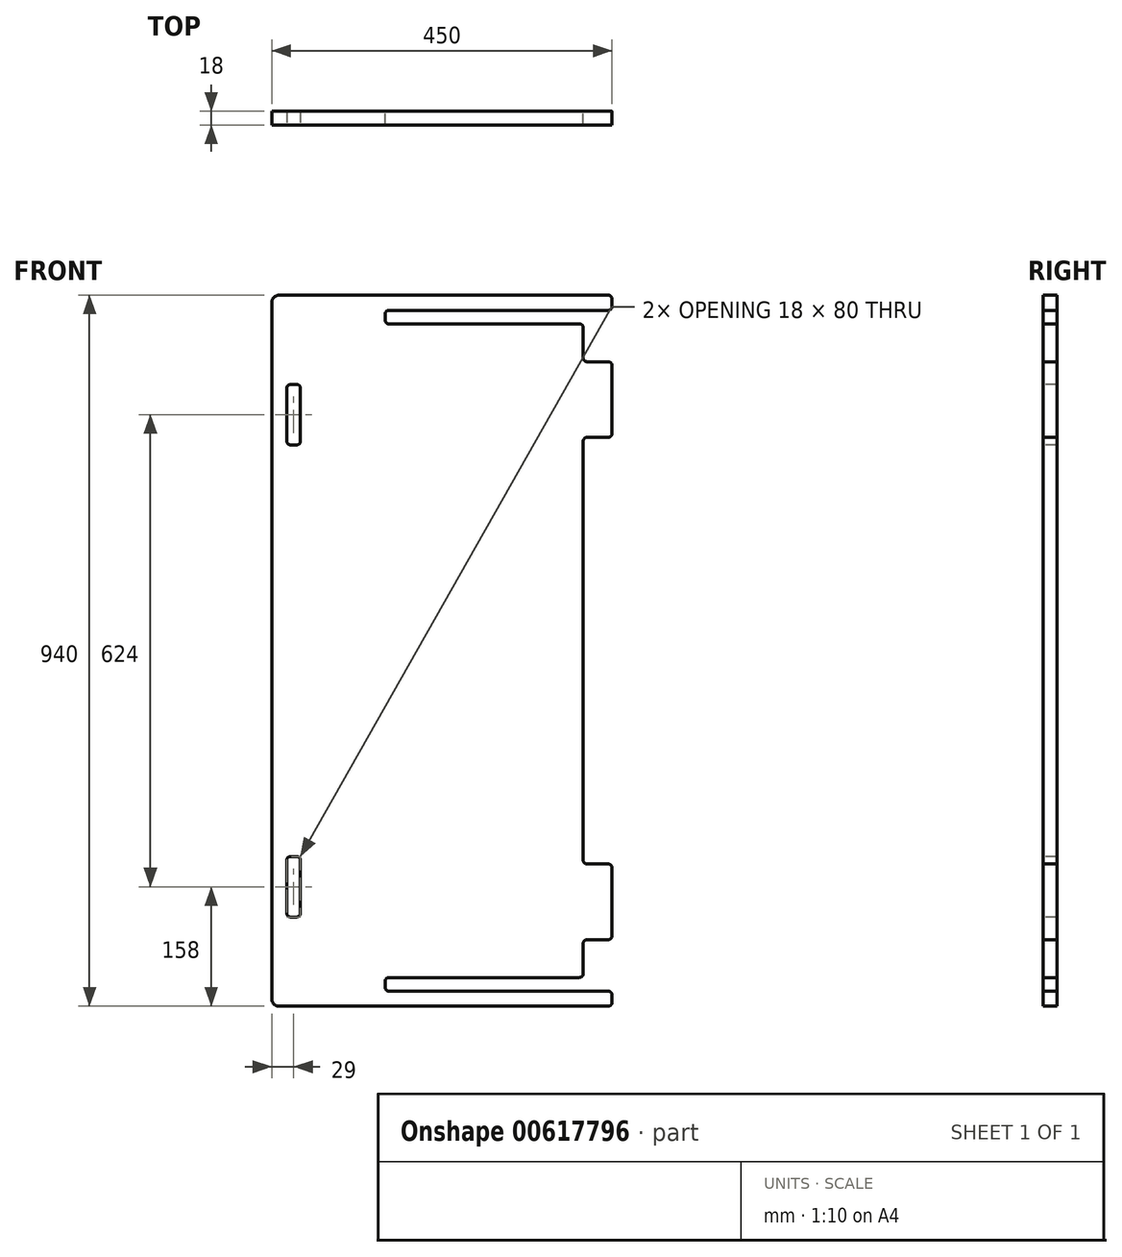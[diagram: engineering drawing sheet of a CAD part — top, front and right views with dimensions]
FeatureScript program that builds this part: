
annotation { "Feature Type Name" : "Feature", "Feature Type Description" : "" }
export const myFeature = defineFeature(function(context is Context, id is Id, definition is map)
    precondition{}
    {
        {
            var Q0;
            Q0=qCreatedBy(makeId("Front.planeOp"),FACE);
            var sketch = newSketch(context, id + "F0", { "sketchPlane" : qUnion([Q0])});
            skLineSegment(sketch, "E0", {"start": v(0, 0) * mm, "end": v(0, 940) * mm});
            skLineSegment(sketch, "E1", {"start": v(0, 940) * mm, "end": v(450, 940) * mm});
            skLineSegment(sketch, "E2", {"start": v(450, 940) * mm, "end": v(450, 920) * mm});
            skLineSegment(sketch, "E3", {"start": v(450, 920) * mm, "end": v(150, 920) * mm});
            skLineSegment(sketch, "E4", {"start": v(150, 920) * mm, "end": v(150, 902) * mm});
            skLineSegment(sketch, "E5", {"start": v(150, 902) * mm, "end": v(412, 902) * mm});
            skLineSegment(sketch, "E6", {"start": v(450, 852) * mm, "end": v(450, 752) * mm});
            skLineSegment(sketch, "E7", {"start": v(450, 752) * mm, "end": v(412, 752) * mm});
            skLineSegment(sketch, "E8", {"start": v(412, 752) * mm, "end": v(412, 188) * mm});
            skLineSegment(sketch, "E9", {"start": v(412, 188) * mm, "end": v(450, 188) * mm});
            skLineSegment(sketch, "E10", {"start": v(450, 188) * mm, "end": v(450, 88) * mm});
            skLineSegment(sketch, "E11", {"start": v(412, 38) * mm, "end": v(150, 38) * mm});
            skLineSegment(sketch, "E12", {"start": v(150, 38) * mm, "end": v(150, 20) * mm});
            skLineSegment(sketch, "E13", {"start": v(150, 20) * mm, "end": v(450, 20) * mm});
            skLineSegment(sketch, "E14", {"start": v(450, 20) * mm, "end": v(450, 0) * mm});
            skLineSegment(sketch, "E15", {"start": v(450, 0) * mm, "end": v(0, 0) * mm});
            skLineSegment(sketch, "E16", {"start": v(450, 852) * mm, "end": v(412, 852) * mm});
            skLineSegment(sketch, "E17", {"start": v(412, 852) * mm, "end": v(412, 902) * mm});
            skPoint(sketch, "E18.orphan", {"position": v(450, 902) * mm});
            skLineSegment(sketch, "E19", {"start": v(450, 88) * mm, "end": v(412, 88) * mm});
            skLineSegment(sketch, "E20", {"start": v(412, 88) * mm, "end": v(412, 38) * mm});
            skPoint(sketch, "E21.orphan", {"position": v(450, 38) * mm});
            skSolve(sketch);
        }
        {
            var Q0;
            Q0=makeQuery(id+"F0.imprint","IMPRINT",FACE,{"disambiguationData":[TD([[makeQuery(id+"F0.imprint","IMPRINT",EDGE,{"derivedFrom":sQuery(id+"F0.wireOp",EDGE,"E0")}),-1.0]])]});
            extrude(context, id + "F1", {"entities" : qUnion([Q0]), "depth" : 18 * mm, "offsetDistance" : 25 * mm});
        }
        {
            var Q0;
            Q0=makeQuery(id+"F1.opExtrude","CAP_FACE",FACE,{"disambiguationData":[OSD([sQuery(id+"F0.wireOp",EDGE,"E0"),sQuery(id+"F0.wireOp",EDGE,"E1"),sQuery(id+"F0.wireOp",EDGE,"E2"),sQuery(id+"F0.wireOp",EDGE,"E3"),sQuery(id+"F0.wireOp",EDGE,"E4"),sQuery(id+"F0.wireOp",EDGE,"E5"),sQuery(id+"F0.wireOp",EDGE,"E6"),sQuery(id+"F0.wireOp",EDGE,"E7"),sQuery(id+"F0.wireOp",EDGE,"E8"),sQuery(id+"F0.wireOp",EDGE,"E9"),sQuery(id+"F0.wireOp",EDGE,"E10"),sQuery(id+"F0.wireOp",EDGE,"E11"),sQuery(id+"F0.wireOp",EDGE,"E12"),sQuery(id+"F0.wireOp",EDGE,"E13"),sQuery(id+"F0.wireOp",EDGE,"E14"),sQuery(id+"F0.wireOp",EDGE,"E15")])],"isStart":false});
            var sketch = newSketch(context, id + "F2", { "sketchPlane" : qUnion([Q0])});
            skLineSegment(sketch, "E22.bottom", {"start": v(20, 822) * mm, "end": v(38, 822) * mm});
            skLineSegment(sketch, "E22.top", {"start": v(20, 742) * mm, "end": v(38, 742) * mm});
            skLineSegment(sketch, "E22.left", {"start": v(20, 822) * mm, "end": v(20, 742) * mm});
            skLineSegment(sketch, "E22.right", {"start": v(38, 822) * mm, "end": v(38, 742) * mm});
            skLineSegment(sketch, "E23.bottom", {"start": v(20, 198) * mm, "end": v(38, 198) * mm});
            skLineSegment(sketch, "E23.top", {"start": v(20, 118) * mm, "end": v(38, 118) * mm});
            skLineSegment(sketch, "E23.left", {"start": v(20, 198) * mm, "end": v(20, 118) * mm});
            skLineSegment(sketch, "E23.right", {"start": v(38, 198) * mm, "end": v(38, 118) * mm});
            skSolve(sketch);
        }
        {
            var Q0;
            Q0=makeQuery(id+"F2.imprint","IMPRINT",FACE,{"disambiguationData":[TD([[makeQuery(id+"F2.imprint","IMPRINT",EDGE,{"derivedFrom":sQuery(id+"F2.wireOp",EDGE,"E22.bottom")}),-1.0]])]});
            var Q1;
            Q1=makeQuery(id+"F2.imprint","IMPRINT",FACE,{"disambiguationData":[TD([[makeQuery(id+"F2.imprint","IMPRINT",EDGE,{"derivedFrom":sQuery(id+"F2.wireOp",EDGE,"E23.bottom")}),-1.0]])]});
            extrude(context, id + "F3", {"entities" : qUnion([Q0, Q1]), "operationType" : NewBodyOperationType.REMOVE, "oppositeDirection" : true, "depth" : 25 * mm, "offsetDistance" : 25 * mm});
        }
        {
            var Q0;
            Q0=makeQuery(id+"F1.opExtrude","SWEPT_EDGE",EDGE,{"disambiguationData":[OSD([sQuery(id+"F0.wireOp",EDGE,"E0"),sQuery(id+"F0.wireOp",EDGE,"E15")])]});
            var Q1;
            Q1=makeQuery(id+"F1.opExtrude","SWEPT_EDGE",EDGE,{"disambiguationData":[OSD([sQuery(id+"F0.wireOp",EDGE,"E0"),sQuery(id+"F0.wireOp",EDGE,"E1")])]});
            fillet(context, id + "F4", {"entities" : qUnion([Q0, Q1]), "radius" : 10 * mm, "tangentPropagation" : true, "allowEdgeOverflow" : false});
        }
        {
            var Q0;
            Q0=makeQuery(id+"F3.boolean.opBoolean","COPY",EDGE,{"derivedFrom":makeQuery(id+"F3.opExtrude","SWEPT_EDGE",EDGE,{"disambiguationData":[OSD([sQuery(id+"F2.wireOp",EDGE,"E22.bottom"),sQuery(id+"F2.wireOp",EDGE,"E22.left")])]})});
            var Q1;
            Q1=makeQuery(id+"F3.boolean.opBoolean","COPY",EDGE,{"derivedFrom":makeQuery(id+"F3.opExtrude","SWEPT_EDGE",EDGE,{"disambiguationData":[OSD([sQuery(id+"F2.wireOp",EDGE,"E22.bottom"),sQuery(id+"F2.wireOp",EDGE,"E22.right")])]})});
            var Q2;
            Q2=makeQuery(id+"F3.boolean.opBoolean","COPY",EDGE,{"derivedFrom":makeQuery(id+"F3.opExtrude","SWEPT_EDGE",EDGE,{"disambiguationData":[OSD([sQuery(id+"F2.wireOp",EDGE,"E22.top"),sQuery(id+"F2.wireOp",EDGE,"E22.left")])]})});
            var Q3;
            Q3=makeQuery(id+"F3.boolean.opBoolean","COPY",EDGE,{"derivedFrom":makeQuery(id+"F3.opExtrude","SWEPT_EDGE",EDGE,{"disambiguationData":[OSD([sQuery(id+"F2.wireOp",EDGE,"E22.top"),sQuery(id+"F2.wireOp",EDGE,"E22.right")])]})});
            fillet(context, id + "F5", {"entities" : qUnion([Q0, Q1, Q2, Q3]), "radius" : 5 * mm, "tangentPropagation" : true, "allowEdgeOverflow" : false});
        }
        {
            var Q0;
            Q0=makeQuery(id+"F3.boolean.opBoolean","COPY",EDGE,{"derivedFrom":makeQuery(id+"F3.opExtrude","SWEPT_EDGE",EDGE,{"disambiguationData":[OSD([sQuery(id+"F2.wireOp",EDGE,"E23.bottom"),sQuery(id+"F2.wireOp",EDGE,"E23.right")])]})});
            var Q1;
            Q1=makeQuery(id+"F3.boolean.opBoolean","COPY",EDGE,{"derivedFrom":makeQuery(id+"F3.opExtrude","SWEPT_EDGE",EDGE,{"disambiguationData":[OSD([sQuery(id+"F2.wireOp",EDGE,"E23.bottom"),sQuery(id+"F2.wireOp",EDGE,"E23.left")])]})});
            var Q2;
            Q2=makeQuery(id+"F3.boolean.opBoolean","COPY",EDGE,{"derivedFrom":makeQuery(id+"F3.opExtrude","SWEPT_EDGE",EDGE,{"disambiguationData":[OSD([sQuery(id+"F2.wireOp",EDGE,"E23.top"),sQuery(id+"F2.wireOp",EDGE,"E23.left")])]})});
            var Q3;
            Q3=makeQuery(id+"F3.boolean.opBoolean","COPY",EDGE,{"derivedFrom":makeQuery(id+"F3.opExtrude","SWEPT_EDGE",EDGE,{"disambiguationData":[OSD([sQuery(id+"F2.wireOp",EDGE,"E23.top"),sQuery(id+"F2.wireOp",EDGE,"E23.right")])]})});
            fillet(context, id + "F6", {"entities" : qUnion([Q0, Q1, Q2, Q3]), "radius" : 5 * mm, "tangentPropagation" : true, "allowEdgeOverflow" : false});
        }
        {
            var Q0;
            Q0=makeQuery(id+"F1.opExtrude","SWEPT_EDGE",EDGE,{"disambiguationData":[OSD([sQuery(id+"F0.wireOp",EDGE,"E14"),sQuery(id+"F0.wireOp",EDGE,"E15")])]});
            var Q1;
            Q1=makeQuery(id+"F1.opExtrude","SWEPT_EDGE",EDGE,{"disambiguationData":[OSD([sQuery(id+"F0.wireOp",EDGE,"E13"),sQuery(id+"F0.wireOp",EDGE,"E14")])]});
            var Q2;
            Q2=makeQuery(id+"F1.opExtrude","SWEPT_EDGE",EDGE,{"disambiguationData":[OSD([sQuery(id+"F0.wireOp",EDGE,"E10"),sQuery(id+"F0.wireOp",EDGE,"E11")])]});
            var Q3;
            Q3=makeQuery(id+"F1.opExtrude","SWEPT_EDGE",EDGE,{"disambiguationData":[OSD([sQuery(id+"F0.wireOp",EDGE,"E11"),sQuery(id+"F0.wireOp",EDGE,"E12")])]});
            var Q4;
            Q4=makeQuery(id+"F1.opExtrude","SWEPT_EDGE",EDGE,{"disambiguationData":[OSD([sQuery(id+"F0.wireOp",EDGE,"E12"),sQuery(id+"F0.wireOp",EDGE,"E13")])]});
            fillet(context, id + "F7", {"entities" : qUnion([Q0, Q1, Q2, Q3, Q4]), "radius" : 5 * mm, "tangentPropagation" : true, "allowEdgeOverflow" : false});
        }
        {
            var Q0;
            Q0=makeQuery(id+"F1.opExtrude","SWEPT_EDGE",EDGE,{"disambiguationData":[OSD([sQuery(id+"F0.wireOp",EDGE,"E9"),sQuery(id+"F0.wireOp",EDGE,"E10")])]});
            var Q1;
            Q1=makeQuery(id+"F1.opExtrude","SWEPT_EDGE",EDGE,{"disambiguationData":[OSD([sQuery(id+"F0.wireOp",EDGE,"E8"),sQuery(id+"F0.wireOp",EDGE,"E9")])]});
            var Q2;
            Q2=makeQuery(id+"F1.opExtrude","SWEPT_EDGE",EDGE,{"disambiguationData":[OSD([sQuery(id+"F0.wireOp",EDGE,"E7"),sQuery(id+"F0.wireOp",EDGE,"E8")])]});
            var Q3;
            Q3=makeQuery(id+"F1.opExtrude","SWEPT_EDGE",EDGE,{"disambiguationData":[OSD([sQuery(id+"F0.wireOp",EDGE,"E6"),sQuery(id+"F0.wireOp",EDGE,"E7")])]});
            fillet(context, id + "F8", {"entities" : qUnion([Q0, Q1, Q2, Q3]), "radius" : 5 * mm, "tangentPropagation" : true, "allowEdgeOverflow" : false});
        }
        {
            var Q0;
            Q0=makeQuery(id+"F1.opExtrude","SWEPT_EDGE",EDGE,{"disambiguationData":[OSD([sQuery(id+"F0.wireOp",EDGE,"E5"),sQuery(id+"F0.wireOp",EDGE,"E6")])]});
            var Q1;
            Q1=makeQuery(id+"F1.opExtrude","SWEPT_EDGE",EDGE,{"disambiguationData":[OSD([sQuery(id+"F0.wireOp",EDGE,"E2"),sQuery(id+"F0.wireOp",EDGE,"E3")])]});
            var Q2;
            Q2=makeQuery(id+"F1.opExtrude","SWEPT_EDGE",EDGE,{"disambiguationData":[OSD([sQuery(id+"F0.wireOp",EDGE,"E1"),sQuery(id+"F0.wireOp",EDGE,"E2")])]});
            var Q3;
            Q3=makeQuery(id+"F1.opExtrude","SWEPT_EDGE",EDGE,{"disambiguationData":[OSD([sQuery(id+"F0.wireOp",EDGE,"E3"),sQuery(id+"F0.wireOp",EDGE,"E4")])]});
            var Q4;
            Q4=makeQuery(id+"F1.opExtrude","SWEPT_EDGE",EDGE,{"disambiguationData":[OSD([sQuery(id+"F0.wireOp",EDGE,"E4"),sQuery(id+"F0.wireOp",EDGE,"E5")])]});
            fillet(context, id + "F9", {"entities" : qUnion([Q0, Q1, Q2, Q3, Q4]), "radius" : 5 * mm, "tangentPropagation" : true, "allowEdgeOverflow" : false});
        }
        {
            var Q0;
            Q0=makeQuery(id+"F1.opExtrude","SWEPT_EDGE",EDGE,{"disambiguationData":[OSD([sQuery(id+"F0.wireOp",EDGE,"E19"),sQuery(id+"F0.wireOp",EDGE,"E20")])]});
            var Q1;
            Q1=makeQuery(id+"F1.opExtrude","SWEPT_EDGE",EDGE,{"disambiguationData":[OSD([sQuery(id+"F0.wireOp",EDGE,"E16"),sQuery(id+"F0.wireOp",EDGE,"E17")])]});
            fillet(context, id + "F10", {"entities" : qUnion([Q0, Q1]), "radius" : 5 * mm, "tangentPropagation" : true, "allowEdgeOverflow" : false});
        }
    });
